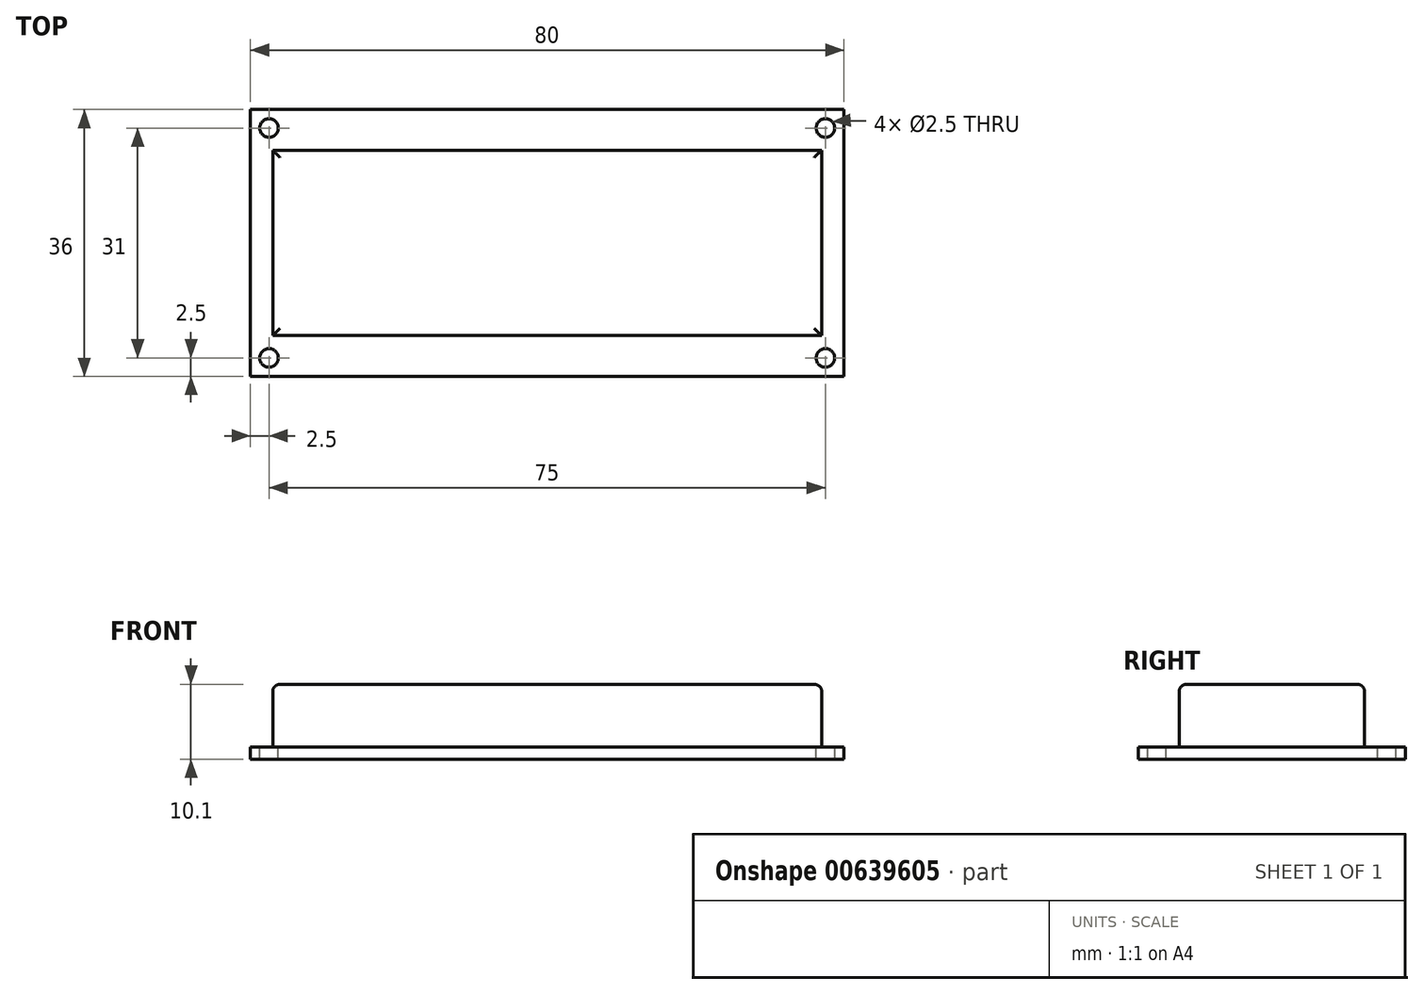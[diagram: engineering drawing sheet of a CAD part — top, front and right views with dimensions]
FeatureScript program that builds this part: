
annotation { "Feature Type Name" : "Feature", "Feature Type Description" : "" }
export const myFeature = defineFeature(function(context is Context, id is Id, definition is map)
    precondition{}
    {
        {
            var Q0;
            Q0=qCreatedBy(makeId("Top.planeOp"),FACE);
            var sketch = newSketch(context, id + "F0", { "sketchPlane" : qUnion([Q0])});
            skLineSegment(sketch, "E0.bottom", {"start": v(-40, -18) * mm, "end": v(40, -18) * mm});
            skLineSegment(sketch, "E0.top", {"start": v(-40, 18) * mm, "end": v(40, 18) * mm});
            skLineSegment(sketch, "E0.left", {"start": v(-40, -18) * mm, "end": v(-40, 18) * mm});
            skLineSegment(sketch, "E0.right", {"start": v(40, -18) * mm, "end": v(40, 18) * mm});
            skPoint(sketch, "E0.middle", {"position": v(0, 0) * mm});
            skLineSegment(sketch, "E1.bottom", {"start": v(37, -12.5) * mm, "end": v(-37, -12.5) * mm});
            skLineSegment(sketch, "E1.top", {"start": v(37, 12.5) * mm, "end": v(-37, 12.5) * mm});
            skLineSegment(sketch, "E1.left", {"start": v(37, -12.5) * mm, "end": v(37, 12.5) * mm});
            skLineSegment(sketch, "E1.right", {"start": v(-37, -12.5) * mm, "end": v(-37, 12.5) * mm});
            skPoint(sketch, "E2", {"position": v(-37.5, 15.5) * mm});
            skPoint(sketch, "E3.MirrorP", {"position": v(37.5, 15.5) * mm});
            skPoint(sketch, "E4.MirrorP", {"position": v(37.5, -15.5) * mm});
            skPoint(sketch, "E5.MirrorP", {"position": v(-37.5, -15.5) * mm});
            skSolve(sketch);
        }
        {
            var Q0;
            Q0=makeQuery(id+"F0.imprint","IMPRINT",FACE,{"disambiguationData":[TD([[makeQuery(id+"F0.imprint","IMPRINT",EDGE,{"derivedFrom":sQuery(id+"F0.wireOp",EDGE,"E0.bottom")}),1.0]])]});
            var Q1;
            Q1=makeQuery(id+"F0.imprint","IMPRINT",FACE,{"disambiguationData":[TD([[makeQuery(id+"F0.imprint","IMPRINT",EDGE,{"derivedFrom":sQuery(id+"F0.wireOp",EDGE,"E1.bottom")}),-1.0]])]});
            extrude(context, id + "F1", {"entities" : qUnion([Q0, Q1]), "oppositeDirection" : true, "depth" : 1.6 * mm, "offsetDistance" : 25 * mm});
        }
        {
            var Q0;
            Q0=makeQuery(id+"F0.imprint","IMPRINT",FACE,{"disambiguationData":[TD([[makeQuery(id+"F0.imprint","IMPRINT",EDGE,{"derivedFrom":sQuery(id+"F0.wireOp",EDGE,"E1.bottom")}),-1.0]])]});
            extrude(context, id + "F2", {"entities" : qUnion([Q0]), "operationType" : NewBodyOperationType.ADD, "depth" : 8.5 * mm, "offsetDistance" : 25 * mm});
        }
        {
            var Q0;
            Q0=sQuery(id+"F0.wireOp",VERTEX,"E2");
            var Q1;
            Q1=sQuery(id+"F0.wireOp",VERTEX,"E3.MirrorP");
            var Q2;
            Q2=sQuery(id+"F0.wireOp",VERTEX,"E4.MirrorP");
            var Q3;
            Q3=sQuery(id+"F0.wireOp",VERTEX,"E5.MirrorP");
            var Q4;
            Q4=makeQuery(id+"F1.opExtrude","SWEPT_BODY",BODY,{"disambiguationData":[OSD([sQuery(id+"F0.wireOp",EDGE,"E0.bottom"),sQuery(id+"F0.wireOp",EDGE,"E0.top"),sQuery(id+"F0.wireOp",EDGE,"E0.left"),sQuery(id+"F0.wireOp",EDGE,"E0.right")])]});
            hole(context, id + "F3", {"style" : HoleStyle.SIMPLE, "endStyle" : HoleEndStyle.THROUGH, "holeDiameter" : 2.5 * mm, "majorDiameter" : 5 * mm, "isTappedThrough" : true, "tappedDepth" : 12 * mm, "tapClearance" : 3, "locations" : qUnion([Q0, Q1, Q2, Q3]), "scope" : qUnion([Q4])});
        }
        {
            var Q0;
            Q0=makeQuery(id+"F2.opExtrude","CAP_EDGE",EDGE,{"disambiguationData":[OSD([sQuery(id+"F0.wireOp",EDGE,"E1.top")])],"isStart":false});
            var Q1;
            Q1=makeQuery(id+"F2.opExtrude","CAP_EDGE",EDGE,{"disambiguationData":[OSD([sQuery(id+"F0.wireOp",EDGE,"E1.right")])],"isStart":false});
            var Q2;
            Q2=makeQuery(id+"F2.opExtrude","CAP_EDGE",EDGE,{"disambiguationData":[OSD([sQuery(id+"F0.wireOp",EDGE,"E1.bottom")])],"isStart":false});
            var Q3;
            Q3=makeQuery(id+"F2.opExtrude","CAP_EDGE",EDGE,{"disambiguationData":[OSD([sQuery(id+"F0.wireOp",EDGE,"E1.left")])],"isStart":false});
            fillet(context, id + "F4", {"entities" : qUnion([Q0, Q1, Q2, Q3]), "radius" : 1 * mm, "tangentPropagation" : true, "allowEdgeOverflow" : false});
        }
    });
